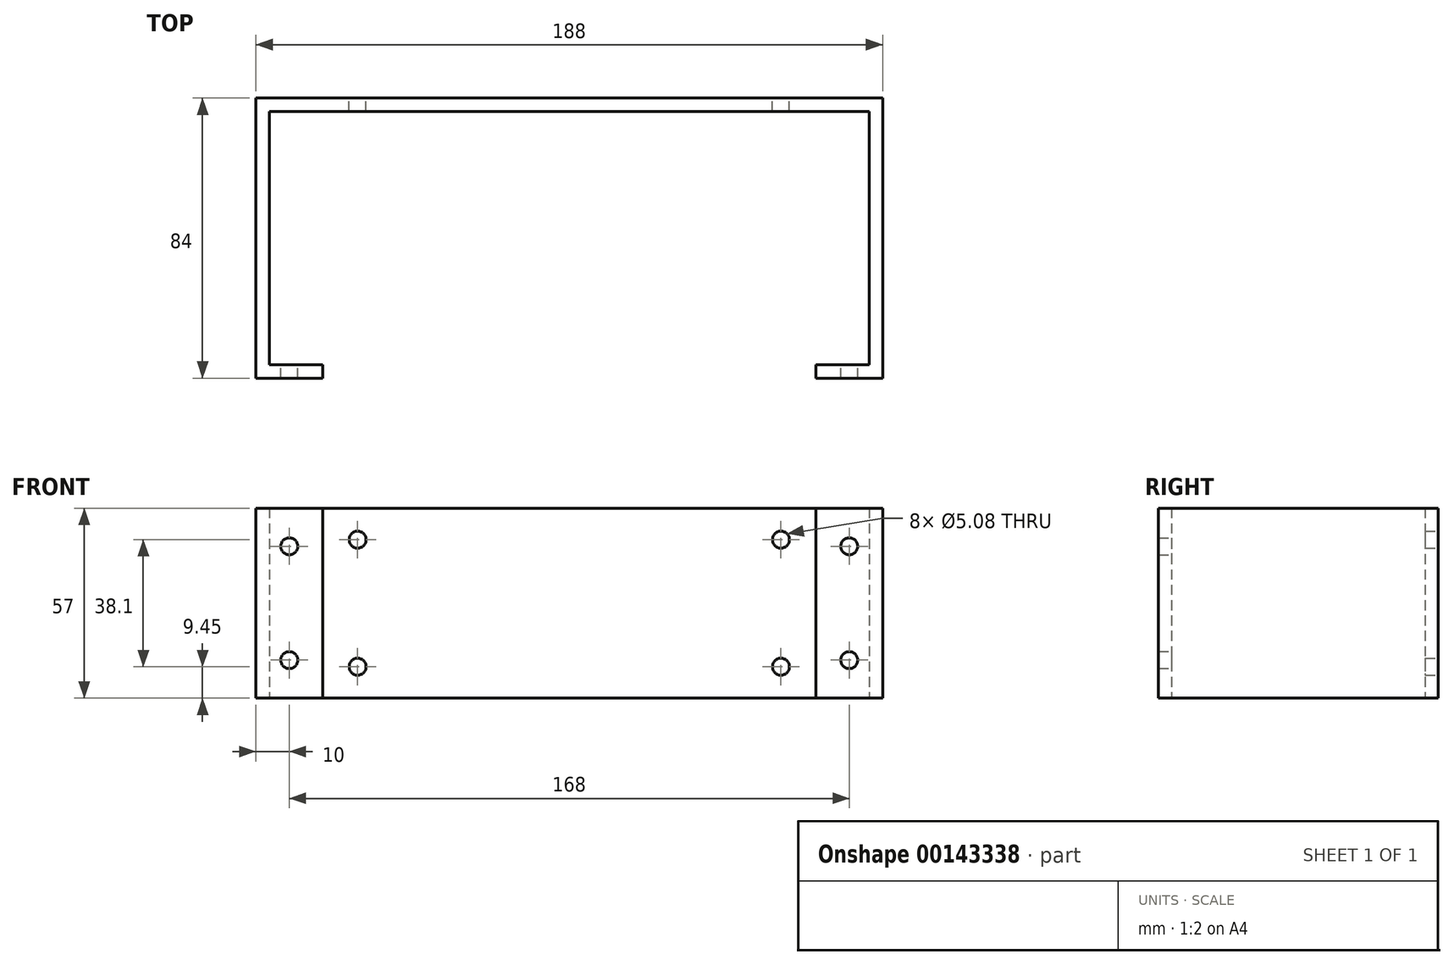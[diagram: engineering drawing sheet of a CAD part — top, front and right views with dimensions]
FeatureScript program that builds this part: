
annotation { "Feature Type Name" : "Feature", "Feature Type Description" : "" }
export const myFeature = defineFeature(function(context is Context, id is Id, definition is map)
    precondition{}
    {
        {
            var Q0;
            Q0=qCreatedBy(makeId("Top.planeOp"),FACE);
            var sketch = newSketch(context, id + "F0", { "sketchPlane" : qUnion([Q0])});
            skLineSegment(sketch, "E0", {"start": v(20, 0) * mm, "end": v(20, 80) * mm});
            skLineSegment(sketch, "E1", {"start": v(20, 80) * mm, "end": v(200, 80) * mm});
            skLineSegment(sketch, "E2", {"start": v(200, 80) * mm, "end": v(200, 0) * mm});
            skLineSegment(sketch, "E3", {"start": v(204, 4) * mm, "end": v(204, 84) * mm});
            skLineSegment(sketch, "E4", {"start": v(204, 84) * mm, "end": v(16, 84) * mm});
            skLineSegment(sketch, "E5", {"start": v(16, 84) * mm, "end": v(16, 4) * mm});
            skLineSegment(sketch, "E6", {"start": v(204, 4) * mm, "end": v(204, 0) * mm});
            skLineSegment(sketch, "E7", {"start": v(204, 0) * mm, "end": v(200, 0) * mm});
            skLineSegment(sketch, "E8.bottom", {"start": v(200, 0) * mm, "end": v(184, 0) * mm});
            skLineSegment(sketch, "E8.top", {"start": v(200, 4) * mm, "end": v(184, 4) * mm});
            skLineSegment(sketch, "E8.left", {"start": v(200, 0) * mm, "end": v(200, 4) * mm});
            skLineSegment(sketch, "E8.right", {"start": v(184, 0) * mm, "end": v(184, 4) * mm});
            skLineSegment(sketch, "E9", {"start": v(16, 4) * mm, "end": v(16, 0) * mm});
            skLineSegment(sketch, "E10", {"start": v(16, 0) * mm, "end": v(20, 0) * mm});
            skLineSegment(sketch, "E11.bottom", {"start": v(20, 0) * mm, "end": v(36, 0) * mm});
            skLineSegment(sketch, "E11.top", {"start": v(20, 4) * mm, "end": v(36, 4) * mm});
            skLineSegment(sketch, "E11.left", {"start": v(20, 0) * mm, "end": v(20, 4) * mm});
            skLineSegment(sketch, "E11.right", {"start": v(36, 0) * mm, "end": v(36, 4) * mm});
            skSolve(sketch);
        }
        {
            var Q0;
            Q0=makeQuery(id+"F0.imprint","IMPRINT",FACE,{"disambiguationData":[TD([[makeQuery(id+"F0.imprint","IMPRINT",EDGE,{"derivedFrom":sQuery(id+"F0.wireOp",EDGE,"E11.bottom")}),1.0]])]});
            var Q1;
            Q1=makeQuery(id+"F0.imprint","IMPRINT",FACE,{"disambiguationData":[TD([[makeQuery(id+"F0.imprint","IMPRINT",EDGE,{"derivedFrom":sQuery(id+"F0.wireOp",EDGE,"E0")}),1.0]])]});
            var Q2;
            Q2=makeQuery(id+"F0.imprint","IMPRINT",FACE,{"disambiguationData":[TD([[makeQuery(id+"F0.imprint","IMPRINT",EDGE,{"derivedFrom":sQuery(id+"F0.wireOp",EDGE,"E8.bottom")}),-1.0]])]});
            extrude(context, id + "F1", {"entities" : qUnion([Q0, Q1, Q2]), "depth" : 57 * mm});
        }
        {
            var Q0;
            Q0=makeQuery(id+"F1.opExtrude","SWEPT_FACE",FACE,{"disambiguationData":[OSD([sQuery(id+"F0.wireOp",EDGE,"E11.top")])]});
            var sketch = newSketch(context, id + "F2", { "sketchPlane" : qUnion([Q0])});
            skLineSegment(sketch, "E12", {"start": v(-36, 57) * mm, "end": v(-36, 45.57) * mm});
            skLineSegment(sketch, "E13", {"start": v(-36, 45.57) * mm, "end": v(-26, 45.57) * mm});
            skCircle(sketch, "E14", {"center": v(-26, 45.57) * mm, "radius": 2.54 * mm});
            skLineSegment(sketch, "E15", {"start": v(-36, 0) * mm, "end": v(-36, 11.43) * mm});
            skLineSegment(sketch, "E16", {"start": v(-36, 11.43) * mm, "end": v(-26, 11.43) * mm});
            skCircle(sketch, "E17", {"center": v(-26, 11.43) * mm, "radius": 2.54 * mm});
            skSolve(sketch);
        }
        {
            var Q0;
            Q0=makeQuery(id+"F1.opExtrude","SWEPT_FACE",FACE,{"disambiguationData":[OSD([sQuery(id+"F0.wireOp",EDGE,"E8.top")])]});
            var sketch = newSketch(context, id + "F3", { "sketchPlane" : qUnion([Q0])});
            skLineSegment(sketch, "E18", {"start": v(-184, 57) * mm, "end": v(-184, 45.57) * mm});
            skLineSegment(sketch, "E19", {"start": v(-184, 45.57) * mm, "end": v(-194, 45.57) * mm});
            skCircle(sketch, "E20", {"center": v(-194, 45.57) * mm, "radius": 2.54 * mm});
            skLineSegment(sketch, "E21", {"start": v(-184, 0) * mm, "end": v(-184, 11.43) * mm});
            skLineSegment(sketch, "E22", {"start": v(-184, 11.43) * mm, "end": v(-194, 11.43) * mm});
            skCircle(sketch, "E23", {"center": v(-194, 11.43) * mm, "radius": 2.54 * mm});
            skSolve(sketch);
        }
        {
            var Q0;
            Q0=makeQuery(id+"F2.imprint","IMPRINT",FACE,{"disambiguationData":[TD([[makeQuery(id+"F2.imprint","IMPRINT",EDGE,{"derivedFrom":sQuery(id+"F2.wireOp",EDGE,"E17")}),1.0]])]});
            var Q1;
            Q1=makeQuery(id+"F2.imprint","IMPRINT",FACE,{"disambiguationData":[TD([[makeQuery(id+"F2.imprint","IMPRINT",EDGE,{"derivedFrom":sQuery(id+"F2.wireOp",EDGE,"E14")}),1.0]])]});
            var Q2;
            Q2=makeQuery(id+"F3.imprint","IMPRINT",FACE,{"disambiguationData":[TD([[makeQuery(id+"F3.imprint","IMPRINT",EDGE,{"derivedFrom":sQuery(id+"F3.wireOp",EDGE,"E23")}),1.0]])]});
            var Q3;
            Q3=makeQuery(id+"F3.imprint","IMPRINT",FACE,{"disambiguationData":[TD([[makeQuery(id+"F3.imprint","IMPRINT",EDGE,{"derivedFrom":sQuery(id+"F3.wireOp",EDGE,"E20")}),1.0]])]});
            extrude(context, id + "F4", {"entities" : qUnion([Q0, Q1, Q2, Q3]), "operationType" : NewBodyOperationType.REMOVE, "endBound" : BoundingType.THROUGH_ALL, "oppositeDirection" : true, "depth" : 25.4 * mm});
        }
        {
            var Q0;
            Q0=makeQuery(id+"F1.opExtrude","SWEPT_FACE",FACE,{"disambiguationData":[OSD([sQuery(id+"F0.wireOp",EDGE,"E4")])]});
            var sketch = newSketch(context, id + "F5", { "sketchPlane" : qUnion([Q0])});
            skLineSegment(sketch, "E24", {"start": v(-204, 0) * mm, "end": v(-74.04, 0) * mm});
            skLineSegment(sketch, "E25", {"start": v(-204, 0) * mm, "end": v(-110, 0) * mm});
            skLineSegment(sketch, "E26", {"start": v(-110, 0) * mm, "end": v(-31.4, 0) * mm});
            skLineSegment(sketch, "E27", {"start": v(-110, 0) * mm, "end": v(-110, 28.5) * mm});
            skPoint(sketch, "E28.middle", {"position": v(-110, 28.5) * mm});
            skCircle(sketch, "E29", {"center": v(-173.5, 47.55) * mm, "radius": 2.54 * mm});
            skCircle(sketch, "E30", {"center": v(-173.5, 9.45) * mm, "radius": 2.54 * mm});
            skCircle(sketch, "E31", {"center": v(-46.5, 47.55) * mm, "radius": 2.54 * mm});
            skCircle(sketch, "E32", {"center": v(-46.5, 9.45) * mm, "radius": 2.54 * mm});
            skSolve(sketch);
        }
        {
            var Q0;
            Q0=makeQuery(id+"F5.imprint","IMPRINT",FACE,{"disambiguationData":[TD([[makeQuery(id+"F5.imprint","IMPRINT",EDGE,{"derivedFrom":sQuery(id+"F5.wireOp",EDGE,"E29")}),1.0]])]});
            var Q1;
            Q1=makeQuery(id+"F5.imprint","IMPRINT",FACE,{"disambiguationData":[TD([[makeQuery(id+"F5.imprint","IMPRINT",EDGE,{"derivedFrom":sQuery(id+"F5.wireOp",EDGE,"E30")}),1.0]])]});
            var Q2;
            Q2=makeQuery(id+"F5.imprint","IMPRINT",FACE,{"disambiguationData":[TD([[makeQuery(id+"F5.imprint","IMPRINT",EDGE,{"derivedFrom":sQuery(id+"F5.wireOp",EDGE,"E32")}),1.0]])]});
            var Q3;
            Q3=makeQuery(id+"F5.imprint","IMPRINT",FACE,{"disambiguationData":[TD([[makeQuery(id+"F5.imprint","IMPRINT",EDGE,{"derivedFrom":sQuery(id+"F5.wireOp",EDGE,"E31")}),1.0]])]});
            extrude(context, id + "F6", {"entities" : qUnion([Q0, Q1, Q2, Q3]), "operationType" : NewBodyOperationType.REMOVE, "endBound" : BoundingType.THROUGH_ALL, "oppositeDirection" : true, "depth" : 25.4 * mm});
        }
    });
